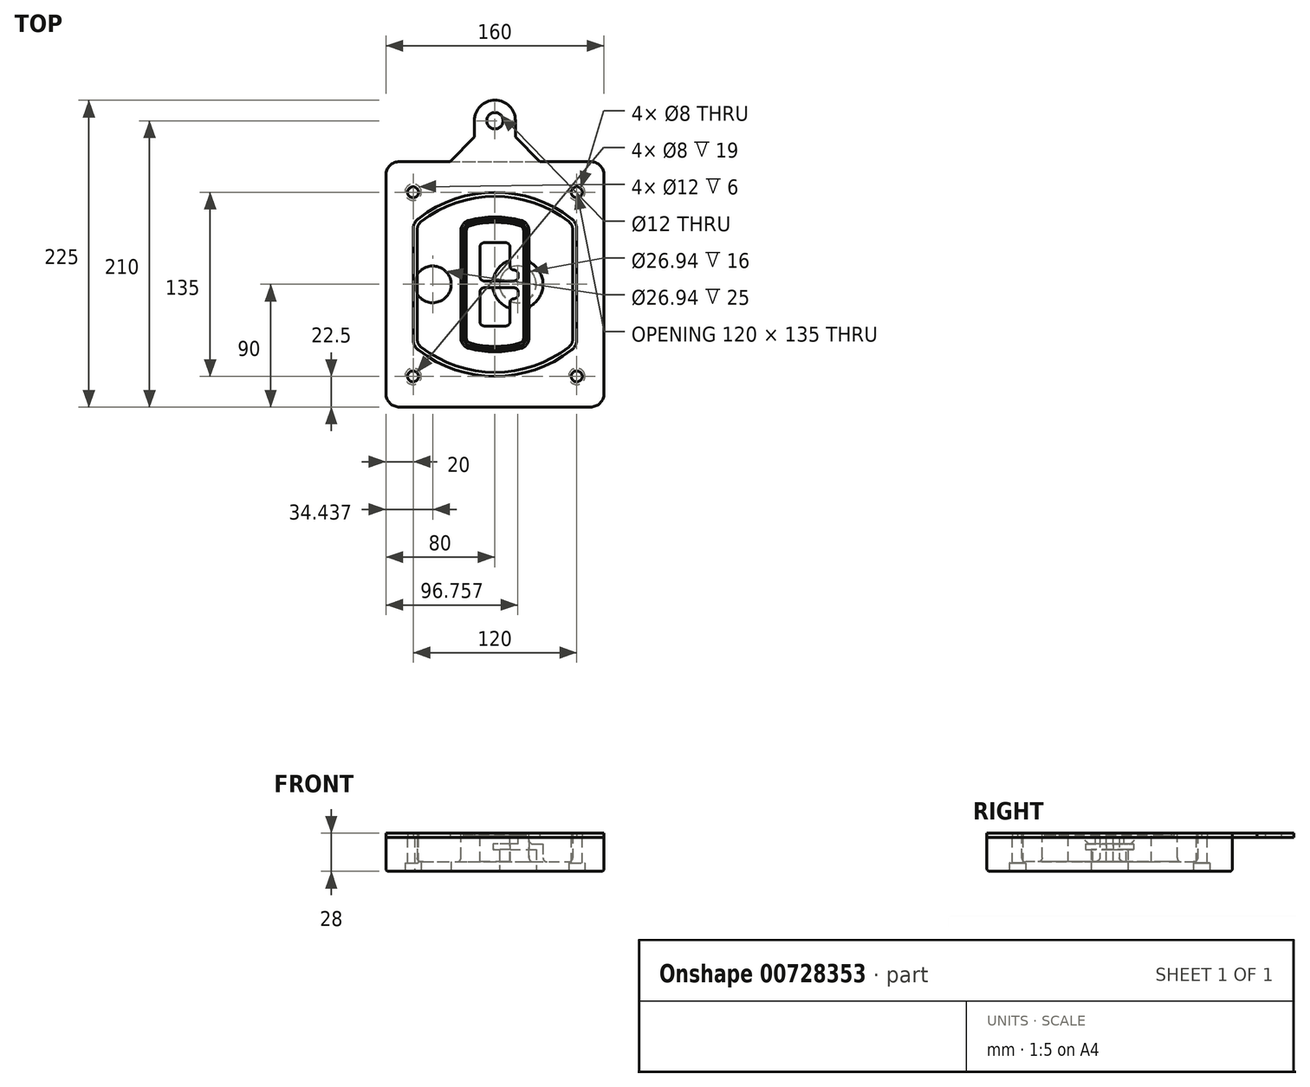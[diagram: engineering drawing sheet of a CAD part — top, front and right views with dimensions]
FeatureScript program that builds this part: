
annotation { "Feature Type Name" : "Feature", "Feature Type Description" : "" }
export const myFeature = defineFeature(function(context is Context, id is Id, definition is map)
    precondition{}
    {
        {
            var Q0;
            Q0=qCreatedBy(makeId("Top.planeOp"),FACE);
            var sketch = newSketch(context, id + "F0", { "sketchPlane" : qUnion([Q0])});
            skPoint(sketch, "E0.rect.middle", {"position": v(0, 0) * mm});
            skLineSegment(sketch, "E1.bottom", {"start": v(-70, -90) * mm, "end": v(70, -90) * mm});
            skLineSegment(sketch, "E1.top", {"start": v(-70, 90) * mm, "end": v(70, 90) * mm});
            skLineSegment(sketch, "E1.left", {"start": v(-80, -80) * mm, "end": v(-80, 80) * mm});
            skLineSegment(sketch, "E1.right", {"start": v(80, -80) * mm, "end": v(80, 80) * mm});
            skLineSegment(sketch, "E2", {"start": v(-80, 90) * mm, "end": v(80, -90) * mm, "construction": true});
            skLineSegment(sketch, "E3", {"start": v(80, 90) * mm, "end": v(-80, -90) * mm, "construction": true});
            skCircle(sketch, "E4", {"center": v(-60, 67.5) * mm, "radius": 4 * mm});
            skCircle(sketch, "E5", {"center": v(60, 67.5) * mm, "radius": 4 * mm});
            skCircle(sketch, "E6", {"center": v(60, -67.5) * mm, "radius": 4 * mm});
            skCircle(sketch, "E7", {"center": v(-60, -67.5) * mm, "radius": 4 * mm});
            skLineSegment(sketch, "E8", {"start": v(-60, 67.5) * mm, "end": v(60, 67.5) * mm, "construction": true});
            skLineSegment(sketch, "E9", {"start": v(60, 67.5) * mm, "end": v(60, -67.5) * mm, "construction": true});
            skLineSegment(sketch, "E10", {"start": v(60, -67.5) * mm, "end": v(-60, -67.5) * mm, "construction": true});
            skLineSegment(sketch, "E11", {"start": v(-60, -67.5) * mm, "end": v(-60, 67.5) * mm, "construction": true});
            skLineSegment(sketch, "E12", {"start": v(-60, 40.3) * mm, "end": v(-60, -40.3) * mm});
            skLineSegment(sketch, "E13", {"start": v(60, 40.3) * mm, "end": v(60, -40.3) * mm});
            skArc(sketch, "E14", {"start": v(56.15, 48.18) * mm, "mid": v(0, 67.5) * mm, "end": v(-56.15, 48.18) * mm});
            skArc(sketch, "E15", {"start": v(-56.15, -48.18) * mm, "mid": v(0, -67.5) * mm, "end": v(56.15, -48.18) * mm});
            skLineSegment(sketch, "E16", {"start": v(-60, 0) * mm, "end": v(60, 0) * mm, "construction": true});
            skPoint(sketch, "E17.visualSharp", {"position": v(-60, -45) * mm});
            skArc(sketch, "E17.filletArc", {"start": v(-60, -40.3) * mm, "mid": v(-58.99, -44.68) * mm, "end": v(-56.15, -48.18) * mm});
            skPoint(sketch, "E18.visualSharp", {"position": v(-60, 45) * mm});
            skArc(sketch, "E18.filletArc", {"start": v(-56.15, 48.18) * mm, "mid": v(-58.99, 44.68) * mm, "end": v(-60, 40.3) * mm});
            skPoint(sketch, "E19.visualSharp", {"position": v(60, 45) * mm});
            skArc(sketch, "E19.filletArc", {"start": v(60, 40.3) * mm, "mid": v(58.99, 44.68) * mm, "end": v(56.15, 48.18) * mm});
            skPoint(sketch, "E20.visualSharp", {"position": v(60, -45) * mm});
            skArc(sketch, "E20.filletArc", {"start": v(56.15, -48.18) * mm, "mid": v(58.99, -44.68) * mm, "end": v(60, -40.3) * mm});
            skPoint(sketch, "E21.visualSharp", {"position": v(-80, 90) * mm});
            skArc(sketch, "E21.filletArc", {"start": v(-70, 90) * mm, "mid": v(-77.07, 87.07) * mm, "end": v(-80, 80) * mm});
            skPoint(sketch, "E22.visualSharp", {"position": v(80, 90) * mm});
            skArc(sketch, "E22.filletArc", {"start": v(80, 80) * mm, "mid": v(77.07, 87.07) * mm, "end": v(70, 90) * mm});
            skPoint(sketch, "E23.visualSharp", {"position": v(80, -90) * mm});
            skArc(sketch, "E23.filletArc", {"start": v(70, -90) * mm, "mid": v(77.07, -87.07) * mm, "end": v(80, -80) * mm});
            skPoint(sketch, "E24.visualSharp", {"position": v(-80, -90) * mm});
            skArc(sketch, "E24.filletArc", {"start": v(-80, -80) * mm, "mid": v(-77.07, -87.07) * mm, "end": v(-70, -90) * mm});
            skArc(sketch, "E25.0", {"start": v(57, 40.3) * mm, "mid": v(56.3, 43.36) * mm, "end": v(54.3, 45.81) * mm});
            skLineSegment(sketch, "E25.1", {"start": v(57, 40.3) * mm, "end": v(57, -40.3) * mm});
            skArc(sketch, "E25.2", {"start": v(54.3, -45.81) * mm, "mid": v(56.3, -43.36) * mm, "end": v(57, -40.3) * mm});
            skArc(sketch, "E25.3", {"start": v(-54.3, -45.81) * mm, "mid": v(0, -64.5) * mm, "end": v(54.3, -45.81) * mm});
            skArc(sketch, "E25.4", {"start": v(-57, -40.3) * mm, "mid": v(-56.3, -43.36) * mm, "end": v(-54.3, -45.81) * mm});
            skArc(sketch, "E25.5", {"start": v(54.3, 45.81) * mm, "mid": v(0, 64.5) * mm, "end": v(-54.3, 45.81) * mm});
            skLineSegment(sketch, "E25.6", {"start": v(-57, 40.3) * mm, "end": v(-57, -40.3) * mm});
            skArc(sketch, "E25.7", {"start": v(-54.3, 45.81) * mm, "mid": v(-56.3, 43.36) * mm, "end": v(-57, 40.3) * mm});
            skArc(sketch, "E26.0", {"start": v(-58.62, 51.33) * mm, "mid": v(-62.58, 46.43) * mm, "end": v(-64, 40.3) * mm});
            skArc(sketch, "E26.1", {"start": v(58.62, 51.33) * mm, "mid": v(0, 71.5) * mm, "end": v(-58.62, 51.33) * mm});
            skArc(sketch, "E26.2", {"start": v(64, 40.3) * mm, "mid": v(62.58, 46.43) * mm, "end": v(58.62, 51.33) * mm});
            skLineSegment(sketch, "E26.3", {"start": v(64, 40.3) * mm, "end": v(64, -40.3) * mm});
            skArc(sketch, "E26.4", {"start": v(58.62, -51.33) * mm, "mid": v(62.58, -46.43) * mm, "end": v(64, -40.3) * mm});
            skLineSegment(sketch, "E26.5", {"start": v(-64, 40.3) * mm, "end": v(-64, -40.3) * mm});
            skArc(sketch, "E26.6", {"start": v(-58.62, -51.33) * mm, "mid": v(0, -71.5) * mm, "end": v(58.62, -51.33) * mm});
            skArc(sketch, "E26.7", {"start": v(-64, -40.3) * mm, "mid": v(-62.58, -46.43) * mm, "end": v(-58.62, -51.33) * mm});
            skSolve(sketch);
        }
        {
            var Q0;
            Q0=makeQuery(id+"F0.imprint","IMPRINT",FACE,{"disambiguationData":[TD([[makeQuery(id+"F0.imprint","IMPRINT",EDGE,{"derivedFrom":sQuery(id+"F0.wireOp",EDGE,"E1.bottom")}),1.0]])]});
            var Q1;
            Q1=makeQuery(id+"F0.imprint","IMPRINT",FACE,{"disambiguationData":[TD([[makeQuery(id+"F0.imprint","IMPRINT",EDGE,{"derivedFrom":sQuery(id+"F0.wireOp",EDGE,"E12")}),1.0]])]});
            var Q2;
            Q2=makeQuery(id+"F0.imprint","IMPRINT",FACE,{"disambiguationData":[TD([[makeQuery(id+"F0.imprint","IMPRINT",EDGE,{"derivedFrom":sQuery(id+"F0.wireOp",EDGE,"E25.0")}),1.0]])]});
            var Q3;
            Q3=makeQuery(id+"F0.imprint","IMPRINT",FACE,{"disambiguationData":[TD([[makeQuery(id+"F0.imprint","IMPRINT",EDGE,{"derivedFrom":sQuery(id+"F0.wireOp",EDGE,"E12")}),-1.0]])]});
            extrude(context, id + "F1", {"entities" : qUnion([Q0, Q1, Q2, Q3]), "oppositeDirection" : true, "depth" : 25 * mm});
        }
        {
            var Q0;
            Q0=makeQuery(id+"F0.imprint","IMPRINT",FACE,{"disambiguationData":[TD([[makeQuery(id+"F0.imprint","IMPRINT",EDGE,{"derivedFrom":sQuery(id+"F0.wireOp",EDGE,"E12")}),1.0]])]});
            extrude(context, id + "F2", {"entities" : qUnion([Q0]), "operationType" : NewBodyOperationType.ADD, "depth" : 3 * mm});
        }
        {
            var Q0;
            Q0=makeQuery(id+"F0.imprint","IMPRINT",FACE,{"disambiguationData":[TD([[makeQuery(id+"F0.imprint","IMPRINT",EDGE,{"derivedFrom":sQuery(id+"F0.wireOp",EDGE,"E25.0")}),1.0]])]});
            extrude(context, id + "F3", {"entities" : qUnion([Q0]), "operationType" : NewBodyOperationType.REMOVE, "oppositeDirection" : true, "depth" : 18 * mm});
        }
        {
            var Q0;
            Q0=makeQuery(id+"F2.opExtrude","CAP_FACE",FACE,{"disambiguationData":[OSD([sQuery(id+"F0.wireOp",EDGE,"E12"),sQuery(id+"F0.wireOp",EDGE,"E13"),sQuery(id+"F0.wireOp",EDGE,"E14"),sQuery(id+"F0.wireOp",EDGE,"E15"),sQuery(id+"F0.wireOp",EDGE,"E17.filletArc"),sQuery(id+"F0.wireOp",EDGE,"E18.filletArc"),sQuery(id+"F0.wireOp",EDGE,"E19.filletArc"),sQuery(id+"F0.wireOp",EDGE,"E20.filletArc"),sQuery(id+"F0.wireOp",EDGE,"E25.0"),sQuery(id+"F0.wireOp",EDGE,"E25.1"),sQuery(id+"F0.wireOp",EDGE,"E25.2"),sQuery(id+"F0.wireOp",EDGE,"E25.3"),sQuery(id+"F0.wireOp",EDGE,"E25.4"),sQuery(id+"F0.wireOp",EDGE,"E25.5"),sQuery(id+"F0.wireOp",EDGE,"E25.6"),sQuery(id+"F0.wireOp",EDGE,"E25.7")])],"isStart":false});
            var sketch = newSketch(context, id + "F4", { "sketchPlane" : qUnion([Q0])});
            skArc(sketch, "E27.0", {"start": v(-19.08, -46.97) * mm, "mid": v(0, -49.5) * mm, "end": v(19.08, -46.97) * mm});
            skArc(sketch, "E28.0", {"start": v(19.08, 46.97) * mm, "mid": v(0, 49.5) * mm, "end": v(-19.08, 46.97) * mm});
            skLineSegment(sketch, "E29", {"start": v(-25, 39.25) * mm, "end": v(-25, -39.25) * mm});
            skLineSegment(sketch, "E30", {"start": v(25, 39.25) * mm, "end": v(25, -39.25) * mm});
            skLineSegment(sketch, "E31", {"start": v(-25, 45.1) * mm, "end": v(25, 45.1) * mm, "construction": true});
            skLineSegment(sketch, "E32", {"start": v(-25, -45.1) * mm, "end": v(25, -45.1) * mm, "construction": true});
            skPoint(sketch, "E33.visualSharp", {"position": v(-25, 45.1) * mm});
            skArc(sketch, "E33.filletArc", {"start": v(-19.08, 46.97) * mm, "mid": v(-23.35, 44.11) * mm, "end": v(-25, 39.25) * mm});
            skPoint(sketch, "E34.visualSharp", {"position": v(25, 45.1) * mm});
            skArc(sketch, "E34.filletArc", {"start": v(25, 39.25) * mm, "mid": v(23.35, 44.11) * mm, "end": v(19.08, 46.97) * mm});
            skPoint(sketch, "E35.visualSharp", {"position": v(25, -45.1) * mm});
            skArc(sketch, "E35.filletArc", {"start": v(19.08, -46.97) * mm, "mid": v(23.35, -44.11) * mm, "end": v(25, -39.25) * mm});
            skPoint(sketch, "E36.visualSharp", {"position": v(-25, -45.1) * mm});
            skArc(sketch, "E36.filletArc", {"start": v(-25, -39.25) * mm, "mid": v(-23.35, -44.11) * mm, "end": v(-19.08, -46.97) * mm});
            skArc(sketch, "E37.0", {"start": v(54.3, 45.81) * mm, "mid": v(0, 64.5) * mm, "end": v(-54.3, 45.81) * mm});
            skArc(sketch, "E37.1", {"start": v(-54.3, 45.81) * mm, "mid": v(-56.3, 43.36) * mm, "end": v(-57, 40.3) * mm});
            skLineSegment(sketch, "E37.2", {"start": v(-57, 40.3) * mm, "end": v(-57, -40.3) * mm});
            skArc(sketch, "E37.3", {"start": v(-57, -40.3) * mm, "mid": v(-56.3, -43.36) * mm, "end": v(-54.3, -45.81) * mm});
            skArc(sketch, "E37.4", {"start": v(-54.3, -45.81) * mm, "mid": v(0, -64.5) * mm, "end": v(54.3, -45.81) * mm});
            skArc(sketch, "E37.5", {"start": v(54.3, -45.81) * mm, "mid": v(56.3, -43.36) * mm, "end": v(57, -40.3) * mm});
            skLineSegment(sketch, "E37.6", {"start": v(57, 40.3) * mm, "end": v(57, -40.3) * mm});
            skArc(sketch, "E37.7", {"start": v(57, 40.3) * mm, "mid": v(56.3, 43.36) * mm, "end": v(54.3, 45.81) * mm});
            skLineSegment(sketch, "E38.0", {"start": v(23, 39.25) * mm, "end": v(23, -39.25) * mm});
            skArc(sketch, "E38.1", {"start": v(18.56, -45.04) * mm, "mid": v(21.76, -42.9) * mm, "end": v(23, -39.25) * mm});
            skArc(sketch, "E38.2", {"start": v(-18.56, -45.04) * mm, "mid": v(0, -47.5) * mm, "end": v(18.56, -45.04) * mm});
            skArc(sketch, "E38.3", {"start": v(-23, -39.25) * mm, "mid": v(-21.76, -42.9) * mm, "end": v(-18.56, -45.04) * mm});
            skLineSegment(sketch, "E38.4", {"start": v(-23, 39.25) * mm, "end": v(-23, -39.25) * mm});
            skArc(sketch, "E38.5", {"start": v(23, 39.25) * mm, "mid": v(21.76, 42.9) * mm, "end": v(18.56, 45.04) * mm});
            skArc(sketch, "E38.6", {"start": v(-18.56, 45.04) * mm, "mid": v(-21.76, 42.9) * mm, "end": v(-23, 39.25) * mm});
            skArc(sketch, "E38.7", {"start": v(18.56, 45.04) * mm, "mid": v(0, 47.5) * mm, "end": v(-18.56, 45.04) * mm});
            skArc(sketch, "E39.0", {"start": v(21, 39.25) * mm, "mid": v(20.18, 41.68) * mm, "end": v(18.04, 43.1) * mm});
            skLineSegment(sketch, "E39.1", {"start": v(21, 39.25) * mm, "end": v(21, -39.25) * mm});
            skArc(sketch, "E39.2", {"start": v(18.04, -43.1) * mm, "mid": v(20.18, -41.68) * mm, "end": v(21, -39.25) * mm});
            skArc(sketch, "E39.3", {"start": v(-18.04, -43.1) * mm, "mid": v(0, -45.5) * mm, "end": v(18.04, -43.1) * mm});
            skArc(sketch, "E39.4", {"start": v(-21, -39.25) * mm, "mid": v(-20.18, -41.68) * mm, "end": v(-18.04, -43.1) * mm});
            skArc(sketch, "E39.5", {"start": v(18.04, 43.1) * mm, "mid": v(0, 45.5) * mm, "end": v(-18.04, 43.1) * mm});
            skLineSegment(sketch, "E39.6", {"start": v(-21, 39.25) * mm, "end": v(-21, -39.25) * mm});
            skArc(sketch, "E39.7", {"start": v(-18.04, 43.1) * mm, "mid": v(-20.18, 41.68) * mm, "end": v(-21, 39.25) * mm});
            skLineSegment(sketch, "E40", {"start": v(-25, 0) * mm, "end": v(25, 0) * mm, "construction": true});
            skLineSegment(sketch, "E41", {"start": v(-11, 5.5) * mm, "end": v(-11, 27.5) * mm});
            skLineSegment(sketch, "E42", {"start": v(-8, 30.5) * mm, "end": v(8, 30.5) * mm});
            skLineSegment(sketch, "E43", {"start": v(11, 27.5) * mm, "end": v(11, 13.5) * mm});
            skLineSegment(sketch, "E44", {"start": v(14, 10.5) * mm, "end": v(14, 10.5) * mm});
            skLineSegment(sketch, "E45", {"start": v(17, 7.5) * mm, "end": v(17, 5.5) * mm});
            skLineSegment(sketch, "E46", {"start": v(14, 2.5) * mm, "end": v(-8, 2.5) * mm});
            skPoint(sketch, "E47.visualSharp", {"position": v(-11, 30.5) * mm});
            skArc(sketch, "E47.filletArc", {"start": v(-8, 30.5) * mm, "mid": v(-10.12, 29.62) * mm, "end": v(-11, 27.5) * mm});
            skPoint(sketch, "E48.visualSharp", {"position": v(11, 30.5) * mm});
            skArc(sketch, "E48.filletArc", {"start": v(11, 27.5) * mm, "mid": v(10.12, 29.62) * mm, "end": v(8, 30.5) * mm});
            skPoint(sketch, "E49.visualSharp", {"position": v(11, 10.5) * mm});
            skArc(sketch, "E49.filletArc", {"start": v(11, 13.5) * mm, "mid": v(11.88, 11.38) * mm, "end": v(14, 10.5) * mm});
            skPoint(sketch, "E50.visualSharp", {"position": v(17, 10.5) * mm});
            skArc(sketch, "E50.filletArc", {"start": v(17, 7.5) * mm, "mid": v(16.12, 9.62) * mm, "end": v(14, 10.5) * mm});
            skPoint(sketch, "E51.visualSharp", {"position": v(17, 2.5) * mm});
            skArc(sketch, "E51.filletArc", {"start": v(14, 2.5) * mm, "mid": v(16.12, 3.38) * mm, "end": v(17, 5.5) * mm});
            skPoint(sketch, "E52.visualSharp", {"position": v(-11, 2.5) * mm});
            skArc(sketch, "E52.filletArc", {"start": v(-11, 5.5) * mm, "mid": v(-10.12, 3.38) * mm, "end": v(-8, 2.5) * mm});
            skLineSegment(sketch, "E53.0.MirrorCS", {"start": v(14, -2.5) * mm, "end": v(-8, -2.5) * mm});
            skArc(sketch, "E54.0.MirrorCS", {"start": v(-11, -5.5) * mm, "mid": v(-10.12, -3.38) * mm, "end": v(-8, -2.5) * mm});
            skLineSegment(sketch, "E55.0.MirrorCS", {"start": v(-11, -5.5) * mm, "end": v(-11, -27.5) * mm});
            skArc(sketch, "E56.0.MirrorCS", {"start": v(-8, -30.5) * mm, "mid": v(-10.12, -29.62) * mm, "end": v(-11, -27.5) * mm});
            skLineSegment(sketch, "E57.0.MirrorCS", {"start": v(-8, -30.5) * mm, "end": v(8, -30.5) * mm});
            skArc(sketch, "E58.0.MirrorCS", {"start": v(11, -27.5) * mm, "mid": v(10.12, -29.62) * mm, "end": v(8, -30.5) * mm});
            skLineSegment(sketch, "E59.0.MirrorCS", {"start": v(11, -27.5) * mm, "end": v(11, -13.5) * mm});
            skArc(sketch, "E60.0.MirrorCS", {"start": v(11, -13.5) * mm, "mid": v(11.88, -11.38) * mm, "end": v(14, -10.5) * mm});
            skArc(sketch, "E61.0.MirrorCS", {"start": v(17, -7.5) * mm, "mid": v(16.12, -9.62) * mm, "end": v(14, -10.5) * mm});
            skLineSegment(sketch, "E62.0.MirrorCS", {"start": v(17, -7.5) * mm, "end": v(17, -5.5) * mm});
            skArc(sketch, "E63.0.MirrorCS", {"start": v(14, -2.5) * mm, "mid": v(16.12, -3.38) * mm, "end": v(17, -5.5) * mm});
            skSolve(sketch);
        }
        {
            var Q0;
            Q0=makeQuery(id+"F4.imprint","IMPRINT",FACE,{"disambiguationData":[TD([[makeQuery(id+"F4.imprint","IMPRINT",EDGE,{"derivedFrom":sQuery(id+"F4.wireOp",EDGE,"E27.0")}),1.0]])]});
            var Q1;
            Q1=makeQuery(id+"F4.imprint","IMPRINT",FACE,{"disambiguationData":[TD([[makeQuery(id+"F4.imprint","IMPRINT",EDGE,{"derivedFrom":sQuery(id+"F4.wireOp",EDGE,"E38.0")}),-1.0]])]});
            var Q2;
            Q2=makeQuery(id+"F4.imprint","IMPRINT",FACE,{"disambiguationData":[TD([[makeQuery(id+"F4.imprint","IMPRINT",EDGE,{"derivedFrom":sQuery(id+"F4.wireOp",EDGE,"E39.0")}),1.0]])]});
            extrude(context, id + "F5", {"entities" : qUnion([Q0, Q1, Q2]), "operationType" : NewBodyOperationType.ADD, "endBound" : BoundingType.UP_TO_NEXT, "oppositeDirection" : true, "depth" : 25 * mm});
        }
        {
            var Q0;
            Q0=makeQuery(id+"F4.imprint","IMPRINT",FACE,{"disambiguationData":[TD([[makeQuery(id+"F4.imprint","IMPRINT",EDGE,{"derivedFrom":sQuery(id+"F4.wireOp",EDGE,"E38.0")}),-1.0]])]});
            extrude(context, id + "F6", {"entities" : qUnion([Q0]), "operationType" : NewBodyOperationType.REMOVE, "oppositeDirection" : true, "depth" : 2 * mm});
        }
        {
            var Q0;
            Q0=makeQuery(id+"F1.opExtrude","CAP_FACE",FACE,{"disambiguationData":[OSD([sQuery(id+"F0.wireOp",EDGE,"E1.bottom"),sQuery(id+"F0.wireOp",EDGE,"E1.top"),sQuery(id+"F0.wireOp",EDGE,"E1.left"),sQuery(id+"F0.wireOp",EDGE,"E1.right"),sQuery(id+"F0.wireOp",EDGE,"E4"),sQuery(id+"F0.wireOp",EDGE,"E5"),sQuery(id+"F0.wireOp",EDGE,"E6"),sQuery(id+"F0.wireOp",EDGE,"E7"),sQuery(id+"F0.wireOp",EDGE,"E21.filletArc"),sQuery(id+"F0.wireOp",EDGE,"E22.filletArc"),sQuery(id+"F0.wireOp",EDGE,"E23.filletArc"),sQuery(id+"F0.wireOp",EDGE,"E24.filletArc")])],"isStart":false});
            var sketch = newSketch(context, id + "F7", { "sketchPlane" : qUnion([Q0])});
            skCircle(sketch, "E64", {"center": v(16.76, 0) * mm, "radius": 13.47 * mm});
            skCircle(sketch, "E65", {"center": v(-45.56, 0) * mm, "radius": 13.47 * mm});
            skLineSegment(sketch, "E66", {"start": v(80, 0) * mm, "end": v(-80, 0) * mm});
            skCircle(sketch, "E67", {"center": v(16.76, 0) * mm, "radius": 18.47 * mm});
            skCircle(sketch, "E68", {"center": v(60, -67.5) * mm, "radius": 6 * mm});
            skCircle(sketch, "E69", {"center": v(-60, -67.5) * mm, "radius": 6 * mm});
            skCircle(sketch, "E70", {"center": v(-60, 67.5) * mm, "radius": 6 * mm});
            skCircle(sketch, "E71", {"center": v(60, 67.5) * mm, "radius": 6 * mm});
            skSolve(sketch);
        }
        {
            var Q0;
            {var subQ1=sQuery(id+"F7.wireOp",EDGE,"E66");var subQ4=sQuery(id+"F7.wireOp",EDGE,"E64");var subQ6=makeQuery(id+"F7.imprint","INTERSECT",VERTEX,{"disambiguationData":[OD(0.0)],"derivedFrom":[subQ4,subQ1]});Q0=makeQuery(id+"F7.imprint","IMPRINT",FACE,{"disambiguationData":[TD([[makeQuery(id+"F7.imprint","IMPRINT",EDGE,{"disambiguationData":[TD([[subQ6,-1.0]])],"derivedFrom":subQ4}),-1.0]])]});}
            var Q1;
            {var subQ0=sQuery(id+"F7.wireOp",EDGE,"E66");var subQ1=sQuery(id+"F7.wireOp",EDGE,"E64");var subQ3=makeQuery(id+"F7.imprint","INTERSECT",VERTEX,{"disambiguationData":[OD(0.0)],"derivedFrom":[subQ1,subQ0]});Q1=makeQuery(id+"F7.imprint","IMPRINT",FACE,{"disambiguationData":[TD([[makeQuery(id+"F7.imprint","IMPRINT",EDGE,{"disambiguationData":[TD([[subQ3,-1.0]])],"derivedFrom":subQ1}),1.0]])]});}
            var Q2;
            {var subQ0=sQuery(id+"F7.wireOp",EDGE,"E66");var subQ1=sQuery(id+"F7.wireOp",EDGE,"E64");var subQ3=makeQuery(id+"F7.imprint","INTERSECT",VERTEX,{"disambiguationData":[OD(0.0)],"derivedFrom":[subQ1,subQ0]});Q2=makeQuery(id+"F7.imprint","IMPRINT",FACE,{"disambiguationData":[TD([[makeQuery(id+"F7.imprint","IMPRINT",EDGE,{"disambiguationData":[TD([[subQ3,1.0]])],"derivedFrom":subQ1}),1.0]])]});}
            var Q3;
            {var subQ1=sQuery(id+"F7.wireOp",EDGE,"E66");var subQ4=sQuery(id+"F7.wireOp",EDGE,"E64");var subQ6=makeQuery(id+"F7.imprint","INTERSECT",VERTEX,{"disambiguationData":[OD(0.0)],"derivedFrom":[subQ4,subQ1]});Q3=makeQuery(id+"F7.imprint","IMPRINT",FACE,{"disambiguationData":[TD([[makeQuery(id+"F7.imprint","IMPRINT",EDGE,{"disambiguationData":[TD([[subQ6,1.0]])],"derivedFrom":subQ4}),-1.0]])]});}
            extrude(context, id + "F8", {"entities" : qUnion([Q0, Q1, Q2, Q3]), "operationType" : NewBodyOperationType.ADD, "oppositeDirection" : true, "depth" : 20 * mm});
        }
        {
            var Q0;
            {var subQ0=sQuery(id+"F7.wireOp",EDGE,"E66");var subQ1=sQuery(id+"F7.wireOp",EDGE,"E64");var subQ3=makeQuery(id+"F7.imprint","INTERSECT",VERTEX,{"disambiguationData":[OD(0.0)],"derivedFrom":[subQ1,subQ0]});Q0=makeQuery(id+"F7.imprint","IMPRINT",FACE,{"disambiguationData":[TD([[makeQuery(id+"F7.imprint","IMPRINT",EDGE,{"disambiguationData":[TD([[subQ3,-1.0]])],"derivedFrom":subQ1}),1.0]])]});}
            var Q1;
            {var subQ0=sQuery(id+"F7.wireOp",EDGE,"E66");var subQ1=sQuery(id+"F7.wireOp",EDGE,"E64");var subQ3=makeQuery(id+"F7.imprint","INTERSECT",VERTEX,{"disambiguationData":[OD(0.0)],"derivedFrom":[subQ1,subQ0]});Q1=makeQuery(id+"F7.imprint","IMPRINT",FACE,{"disambiguationData":[TD([[makeQuery(id+"F7.imprint","IMPRINT",EDGE,{"disambiguationData":[TD([[subQ3,1.0]])],"derivedFrom":subQ1}),1.0]])]});}
            extrude(context, id + "F9", {"entities" : qUnion([Q0, Q1]), "operationType" : NewBodyOperationType.REMOVE, "oppositeDirection" : true, "depth" : 16 * mm});
        }
        {
            var Q0;
            {var subQ0=sQuery(id+"F7.wireOp",EDGE,"E66");var subQ1=sQuery(id+"F7.wireOp",EDGE,"E65");var subQ3=makeQuery(id+"F7.imprint","INTERSECT",VERTEX,{"disambiguationData":[OD(0.0)],"derivedFrom":[subQ1,subQ0]});Q0=makeQuery(id+"F7.imprint","IMPRINT",FACE,{"disambiguationData":[TD([[makeQuery(id+"F7.imprint","IMPRINT",EDGE,{"disambiguationData":[TD([[subQ3,-1.0]])],"derivedFrom":subQ1}),1.0]])]});}
            var Q1;
            {var subQ0=sQuery(id+"F7.wireOp",EDGE,"E66");var subQ1=sQuery(id+"F7.wireOp",EDGE,"E65");var subQ3=makeQuery(id+"F7.imprint","INTERSECT",VERTEX,{"disambiguationData":[OD(0.0)],"derivedFrom":[subQ1,subQ0]});Q1=makeQuery(id+"F7.imprint","IMPRINT",FACE,{"disambiguationData":[TD([[makeQuery(id+"F7.imprint","IMPRINT",EDGE,{"disambiguationData":[TD([[subQ3,1.0]])],"derivedFrom":subQ1}),1.0]])]});}
            extrude(context, id + "F10", {"entities" : qUnion([Q0, Q1]), "operationType" : NewBodyOperationType.REMOVE, "oppositeDirection" : true, "depth" : 25 * mm});
        }
        {
            var Q0;
            Q0=makeQuery(id+"F7.imprint","IMPRINT",FACE,{"disambiguationData":[TD([[makeQuery(id+"F7.imprint","IMPRINT",EDGE,{"derivedFrom":sQuery(id+"F7.wireOp",EDGE,"E68")}),1.0]])]});
            var Q1;
            Q1=makeQuery(id+"F7.imprint","IMPRINT",FACE,{"disambiguationData":[TD([[makeQuery(id+"F7.imprint","IMPRINT",EDGE,{"derivedFrom":makeQuery(id+"F1.opExtrude","CAP_EDGE",EDGE,{"disambiguationData":[OSD([sQuery(id+"F0.wireOp",EDGE,"E5")])],"isStart":false})}),-1.0]])]});
            var Q2;
            Q2=makeQuery(id+"F7.imprint","IMPRINT",FACE,{"disambiguationData":[TD([[makeQuery(id+"F7.imprint","IMPRINT",EDGE,{"derivedFrom":sQuery(id+"F7.wireOp",EDGE,"E69")}),1.0]])]});
            var Q3;
            Q3=makeQuery(id+"F7.imprint","IMPRINT",FACE,{"disambiguationData":[TD([[makeQuery(id+"F7.imprint","IMPRINT",EDGE,{"derivedFrom":makeQuery(id+"F1.opExtrude","CAP_EDGE",EDGE,{"disambiguationData":[OSD([sQuery(id+"F0.wireOp",EDGE,"E4")])],"isStart":false})}),-1.0]])]});
            var Q4;
            Q4=makeQuery(id+"F7.imprint","IMPRINT",FACE,{"disambiguationData":[TD([[makeQuery(id+"F7.imprint","IMPRINT",EDGE,{"derivedFrom":sQuery(id+"F7.wireOp",EDGE,"E70")}),1.0]])]});
            var Q5;
            Q5=makeQuery(id+"F7.imprint","IMPRINT",FACE,{"disambiguationData":[TD([[makeQuery(id+"F7.imprint","IMPRINT",EDGE,{"derivedFrom":makeQuery(id+"F1.opExtrude","CAP_EDGE",EDGE,{"disambiguationData":[OSD([sQuery(id+"F0.wireOp",EDGE,"E7")])],"isStart":false})}),-1.0]])]});
            var Q6;
            Q6=makeQuery(id+"F7.imprint","IMPRINT",FACE,{"disambiguationData":[TD([[makeQuery(id+"F7.imprint","IMPRINT",EDGE,{"derivedFrom":sQuery(id+"F7.wireOp",EDGE,"E71")}),1.0]])]});
            var Q7;
            Q7=makeQuery(id+"F7.imprint","IMPRINT",FACE,{"disambiguationData":[TD([[makeQuery(id+"F7.imprint","IMPRINT",EDGE,{"derivedFrom":makeQuery(id+"F1.opExtrude","CAP_EDGE",EDGE,{"disambiguationData":[OSD([sQuery(id+"F0.wireOp",EDGE,"E6")])],"isStart":false})}),-1.0]])]});
            extrude(context, id + "F11", {"entities" : qUnion([Q0, Q1, Q2, Q3, Q4, Q5, Q6, Q7]), "operationType" : NewBodyOperationType.REMOVE, "oppositeDirection" : true, "depth" : 6 * mm});
        }
        {
            var Q0;
            Q0=makeQuery(id+"F9.boolean.opBoolean","COPY",FACE,{"derivedFrom":makeQuery(id+"F9.opExtrude","CAP_FACE",FACE,{"disambiguationData":[OSD([sQuery(id+"F7.wireOp",EDGE,"E64")])],"isStart":false})});
            var sketch = newSketch(context, id + "F12", { "sketchPlane" : qUnion([Q0])});
            skArc(sketch, "E72.0", {"start": v(11, 17.55) * mm, "mid": v(2.57, 11.82) * mm, "end": v(-1.54, 2.5) * mm});
            skArc(sketch, "E72.1", {"start": v(-1.54, -2.5) * mm, "mid": v(2.57, -11.82) * mm, "end": v(11, -17.55) * mm});
            skLineSegment(sketch, "E73", {"start": v(-1.54, -2.5) * mm, "end": v(14, -2.5) * mm});
            skLineSegment(sketch, "E74.0", {"start": v(14, 2.5) * mm, "end": v(-1.54, 2.5) * mm});
            skArc(sketch, "E74.1", {"start": v(14, 2.5) * mm, "mid": v(16.12, 3.38) * mm, "end": v(17, 5.5) * mm});
            skLineSegment(sketch, "E74.2", {"start": v(17, 7.5) * mm, "end": v(17, 5.5) * mm});
            skArc(sketch, "E74.3", {"start": v(17, 7.5) * mm, "mid": v(16.12, 9.62) * mm, "end": v(14, 10.5) * mm});
            skArc(sketch, "E74.4", {"start": v(11, 13.5) * mm, "mid": v(11.88, 11.38) * mm, "end": v(14, 10.5) * mm});
            skLineSegment(sketch, "E74.5", {"start": v(11, 17.55) * mm, "end": v(11, 13.5) * mm});
            skLineSegment(sketch, "E74.7", {"start": v(14, -2.5) * mm, "end": v(-1.54, -2.5) * mm});
            skArc(sketch, "E74.8", {"start": v(14, -2.5) * mm, "mid": v(16.12, -3.38) * mm, "end": v(17, -5.5) * mm});
            skLineSegment(sketch, "E74.9", {"start": v(17, -7.5) * mm, "end": v(17, -5.5) * mm});
            skArc(sketch, "E74.10", {"start": v(17, -7.5) * mm, "mid": v(16.12, -9.62) * mm, "end": v(14, -10.5) * mm});
            skArc(sketch, "E74.11", {"start": v(11, -13.5) * mm, "mid": v(11.88, -11.38) * mm, "end": v(14, -10.5) * mm});
            skLineSegment(sketch, "E74.12", {"start": v(11, -17.55) * mm, "end": v(11, -13.5) * mm});
            skPoint(sketch, "E75.orphan", {"position": v(11, -27.5) * mm});
            skPoint(sketch, "E76.orphan", {"position": v(-8, -2.5) * mm});
            skPoint(sketch, "E77.orphan", {"position": v(-8, 2.5) * mm});
            skPoint(sketch, "E78.orphan", {"position": v(11, 27.5) * mm});
            skSolve(sketch);
        }
        {
            var Q0;
            {var subQ7=sQuery(id+"F12.wireOp",EDGE,"E72.0");var subQ14=sQuery(id+"F12.wireOp",EDGE,"E72.1");var subQ16=sQuery(id+"F12.wireOp",EDGE,"E74.1");var subQ18=sQuery(id+"F12.wireOp",EDGE,"E74.8");Q0=qUnion([makeQuery(id+"F12.imprint","IMPRINT",FACE,{"disambiguationData":[TD([[makeQuery(id+"F12.imprint","IMPRINT",EDGE,{"derivedFrom":subQ7}),1.0]])]}),makeQuery(id+"F12.imprint","IMPRINT",FACE,{"disambiguationData":[TD([[makeQuery(id+"F12.imprint","IMPRINT",EDGE,{"derivedFrom":subQ14}),1.0]])]}),makeQuery(id+"F12.imprint","IMPRINT",FACE,{"disambiguationData":[TD([[makeQuery(id+"F12.imprint","IMPRINT",EDGE,{"derivedFrom":subQ16}),1.0]])]}),makeQuery(id+"F12.imprint","IMPRINT",FACE,{"disambiguationData":[TD([[makeQuery(id+"F12.imprint","IMPRINT",EDGE,{"derivedFrom":subQ18}),-1.0]])]})]);}
            var Q1;
            Q1=makeQuery(id+"F5.boolean.opBoolean","SPLIT",FACE,{"disambiguationData":[TD([makeQuery(id+"F5.opExtrude","SWEPT_FACE",FACE,{"disambiguationData":[OSD([sQuery(id+"F4.wireOp",EDGE,"E41")])]})])],"derivedFrom":makeQuery(id+"F3.boolean.opBoolean","COPY",FACE,{"derivedFrom":makeQuery(id+"F3.opExtrude","CAP_FACE",FACE,{"disambiguationData":[OSD([sQuery(id+"F0.wireOp",EDGE,"E25.0"),sQuery(id+"F0.wireOp",EDGE,"E25.1"),sQuery(id+"F0.wireOp",EDGE,"E25.2"),sQuery(id+"F0.wireOp",EDGE,"E25.3"),sQuery(id+"F0.wireOp",EDGE,"E25.4"),sQuery(id+"F0.wireOp",EDGE,"E25.5"),sQuery(id+"F0.wireOp",EDGE,"E25.6"),sQuery(id+"F0.wireOp",EDGE,"E25.7")])],"isStart":false})})});
            extrude(context, id + "F13", {"entities" : qUnion([Q0]), "operationType" : NewBodyOperationType.REMOVE, "endBound" : BoundingType.UP_TO_SURFACE, "endBoundEntityFace" : qUnion([Q1]), "depth" : 25 * mm});
        }
        {
            var Q0;
            Q0=makeQuery(id+"F3.boolean.opBoolean","COPY",EDGE,{"derivedFrom":makeQuery(id+"F3.opExtrude","CAP_EDGE",EDGE,{"disambiguationData":[OSD([sQuery(id+"F0.wireOp",EDGE,"E25.6")])],"isStart":false})});
            var Q1;
            Q1=makeQuery(id+"F8.boolean.opBoolean","INTERSECT",EDGE,{"derivedFrom":[makeQuery(id+"F5.opExtrude","SWEPT_FACE",FACE,{"disambiguationData":[OSD([sQuery(id+"F4.wireOp",EDGE,"E30")])]}),makeQuery(id+"F8.opExtrude","CAP_FACE",FACE,{"disambiguationData":[OSD([sQuery(id+"F7.wireOp",EDGE,"E67")])],"isStart":false})]});
            var Q2;
            Q2=makeQuery(id+"F8.boolean.opBoolean","INTERSECT",EDGE,{"disambiguationData":[OD(1.0)],"derivedFrom":[makeQuery(id+"F5.opExtrude","SWEPT_FACE",FACE,{"disambiguationData":[OSD([sQuery(id+"F4.wireOp",EDGE,"E30")])]}),makeQuery(id+"F8.opExtrude","SWEPT_FACE",FACE,{"disambiguationData":[OSD([sQuery(id+"F7.wireOp",EDGE,"E67")])]})]});
            var Q3;
            {var subQ0=sQuery(id+"F4.wireOp",EDGE,"E30");Q3=makeQuery(id+"F8.boolean.opBoolean","SPLIT",EDGE,{"disambiguationData":[TD([makeQuery(id+"F5.opExtrude","SWEPT_FACE",FACE,{"disambiguationData":[OSD([sQuery(id+"F4.wireOp",EDGE,"E35.filletArc")])]})])],"derivedFrom":makeQuery(id+"F5.opExtrude","CAP_EDGE",EDGE,{"disambiguationData":[OSD([subQ0])],"isStart":false})});}
            var Q4;
            {var subQ0=sQuery(id+"F0.wireOp",EDGE,"E25.7");var subQ1=sQuery(id+"F0.wireOp",EDGE,"E25.1");var subQ2=sQuery(id+"F0.wireOp",EDGE,"E25.6");var subQ3=sQuery(id+"F0.wireOp",EDGE,"E25.5");var subQ4=sQuery(id+"F0.wireOp",EDGE,"E25.4");var subQ5=sQuery(id+"F0.wireOp",EDGE,"E25.0");var subQ6=sQuery(id+"F0.wireOp",EDGE,"E25.2");var subQ7=sQuery(id+"F0.wireOp",EDGE,"E25.3");Q4=makeQuery(id+"F8.boolean.opBoolean","INTERSECT",EDGE,{"derivedFrom":[makeQuery(id+"F5.boolean.opBoolean","SPLIT",FACE,{"disambiguationData":[TD([makeQuery(id+"F2.opExtrude","SWEPT_FACE",FACE,{"disambiguationData":[OSD([subQ5])]})])],"derivedFrom":makeQuery(id+"F3.boolean.opBoolean","COPY",FACE,{"derivedFrom":makeQuery(id+"F3.opExtrude","CAP_FACE",FACE,{"disambiguationData":[OSD([subQ5,subQ1,subQ6,subQ7,subQ4,subQ3,subQ2,subQ0])],"isStart":false})})}),makeQuery(id+"F8.opExtrude","SWEPT_FACE",FACE,{"disambiguationData":[OSD([sQuery(id+"F7.wireOp",EDGE,"E67")])]})]});}
            var Q5;
            Q5=makeQuery(id+"F8.boolean.opBoolean","INTERSECT",EDGE,{"disambiguationData":[OD(0.0)],"derivedFrom":[makeQuery(id+"F5.opExtrude","SWEPT_FACE",FACE,{"disambiguationData":[OSD([sQuery(id+"F4.wireOp",EDGE,"E30")])]}),makeQuery(id+"F8.opExtrude","SWEPT_FACE",FACE,{"disambiguationData":[OSD([sQuery(id+"F7.wireOp",EDGE,"E67")])]})]});
            fillet(context, id + "F14", {"entities" : qUnion([Q0, Q1, Q2, Q3, Q4, Q5]), "radius" : 3 * mm, "tangentPropagation" : true, "allowEdgeOverflow" : false});
        }
        {
            var Q0;
            Q0=makeQuery(id+"F1.opExtrude","CAP_EDGE",EDGE,{"disambiguationData":[OSD([sQuery(id+"F0.wireOp",EDGE,"E1.bottom")])],"isStart":false});
            fillet(context, id + "F15", {"entities" : qUnion([Q0]), "radius" : 2 * mm, "tangentPropagation" : true, "allowEdgeOverflow" : false});
        }
        {
            var Q0;
            {var subQ0=sQuery(id+"F0.wireOp",EDGE,"E21.filletArc");var subQ1=sQuery(id+"F0.wireOp",EDGE,"E7");var subQ2=sQuery(id+"F0.wireOp",EDGE,"E6");var subQ3=sQuery(id+"F0.wireOp",EDGE,"E5");var subQ4=sQuery(id+"F0.wireOp",EDGE,"E4");var subQ5=sQuery(id+"F0.wireOp",EDGE,"E22.filletArc");var subQ6=sQuery(id+"F0.wireOp",EDGE,"E1.bottom");var subQ7=sQuery(id+"F0.wireOp",EDGE,"E1.right");var subQ8=sQuery(id+"F0.wireOp",EDGE,"E1.top");var subQ9=sQuery(id+"F0.wireOp",EDGE,"E1.left");var subQ10=sQuery(id+"F0.wireOp",EDGE,"E23.filletArc");var subQ11=sQuery(id+"F0.wireOp",EDGE,"E24.filletArc");Q0=makeQuery(id+"F2.boolean.opBoolean","SPLIT",FACE,{"disambiguationData":[TD([makeQuery(id+"F1.opExtrude","SWEPT_FACE",FACE,{"disambiguationData":[OSD([subQ6])]})])],"derivedFrom":makeQuery(id+"F1.opExtrude","CAP_FACE",FACE,{"disambiguationData":[OSD([subQ6,subQ8,subQ9,subQ7,subQ4,subQ3,subQ2,subQ1,subQ0,subQ5,subQ10,subQ11])],"isStart":true})});}
            var sketch = newSketch(context, id + "F16", { "sketchPlane" : qUnion([Q0])});
            skPoint(sketch, "E79.start.orphan", {"position": v(0, 90) * mm});
            skLineSegment(sketch, "E80", {"start": v(0, 90) * mm, "end": v(0, 120) * mm, "construction": true});
            skCircle(sketch, "E81", {"center": v(0, 120) * mm, "radius": 6 * mm});
            skLineSegment(sketch, "E82", {"start": v(-33, 90) * mm, "end": v(-15, 108) * mm});
            skLineSegment(sketch, "E83", {"start": v(-15, 108) * mm, "end": v(-15, 120) * mm});
            skLineSegment(sketch, "E84", {"start": v(33, 90) * mm, "end": v(15, 108) * mm});
            skLineSegment(sketch, "E85", {"start": v(15, 108) * mm, "end": v(15, 120) * mm});
            skArc(sketch, "E86", {"start": v(15, 120) * mm, "mid": v(0, 135) * mm, "end": v(-15, 120) * mm});
            skLineSegment(sketch, "E87", {"start": v(-80, 0) * mm, "end": v(80, 0) * mm, "construction": true});
            skArc(sketch, "E88.MirrorCS", {"start": v(15, -120) * mm, "mid": v(0, -135) * mm, "end": v(-15, -120) * mm});
            skLineSegment(sketch, "E89.MirrorCS", {"start": v(15, -108) * mm, "end": v(15, -120) * mm});
            skCircle(sketch, "E90.MirrorC", {"center": v(0, -120) * mm, "radius": 6 * mm});
            skLineSegment(sketch, "E91.MirrorCS", {"start": v(-15, -108) * mm, "end": v(-15, -120) * mm});
            skLineSegment(sketch, "E92.MirrorCS", {"start": v(33, -90) * mm, "end": v(15, -108) * mm});
            skLineSegment(sketch, "E93.MirrorCS", {"start": v(-33, -90) * mm, "end": v(-15, -108) * mm});
            skPoint(sketch, "E94.MirrorP", {"position": v(0, -90) * mm});
            skLineSegment(sketch, "E95.MirrorCS", {"start": v(0, -90) * mm, "end": v(0, -120) * mm, "construction": true});
            skSolve(sketch);
        }
        {
            var Q0;
            Q0=makeQuery(id+"F16.imprint","IMPRINT",FACE,{"disambiguationData":[TD([[makeQuery(id+"F16.imprint","IMPRINT",EDGE,{"derivedFrom":sQuery(id+"F16.wireOp",EDGE,"E81")}),-1.0]])]});
            var Q1;
            Q1=makeQuery(id+"F16.imprint","IMPRINT",FACE,{"disambiguationData":[TD([[makeQuery(id+"F16.imprint","IMPRINT",EDGE,{"derivedFrom":sQuery(id+"F16.wireOp",EDGE,"E88.MirrorCS")}),-1.0]])]});
            var Q2;
            Q2=makeQuery(id+"F16.imprint","IMPRINT",FACE,{"disambiguationData":[TD([[makeQuery(id+"F16.imprint","IMPRINT",EDGE,{"derivedFrom":makeQuery(id+"F1.opExtrude","CAP_EDGE",EDGE,{"disambiguationData":[OSD([sQuery(id+"F0.wireOp",EDGE,"E1.left")])],"isStart":true})}),-1.0]])]});
            var Q3;
            Q3=makeQuery(id+"F2.opExtrude","CAP_FACE",FACE,{"disambiguationData":[OSD([sQuery(id+"F0.wireOp",EDGE,"E12"),sQuery(id+"F0.wireOp",EDGE,"E13"),sQuery(id+"F0.wireOp",EDGE,"E14"),sQuery(id+"F0.wireOp",EDGE,"E15"),sQuery(id+"F0.wireOp",EDGE,"E17.filletArc"),sQuery(id+"F0.wireOp",EDGE,"E18.filletArc"),sQuery(id+"F0.wireOp",EDGE,"E19.filletArc"),sQuery(id+"F0.wireOp",EDGE,"E20.filletArc"),sQuery(id+"F0.wireOp",EDGE,"E25.0"),sQuery(id+"F0.wireOp",EDGE,"E25.1"),sQuery(id+"F0.wireOp",EDGE,"E25.2"),sQuery(id+"F0.wireOp",EDGE,"E25.3"),sQuery(id+"F0.wireOp",EDGE,"E25.4"),sQuery(id+"F0.wireOp",EDGE,"E25.5"),sQuery(id+"F0.wireOp",EDGE,"E25.6"),sQuery(id+"F0.wireOp",EDGE,"E25.7")])],"isStart":false});
            extrude(context, id + "F17", {"entities" : qUnion([Q0, Q1, Q2]), "endBound" : BoundingType.UP_TO_SURFACE, "depth" : 25 * mm, "endBoundEntityFace" : qUnion([Q3]), "offsetDistance" : 25 * mm});
        }
    });
